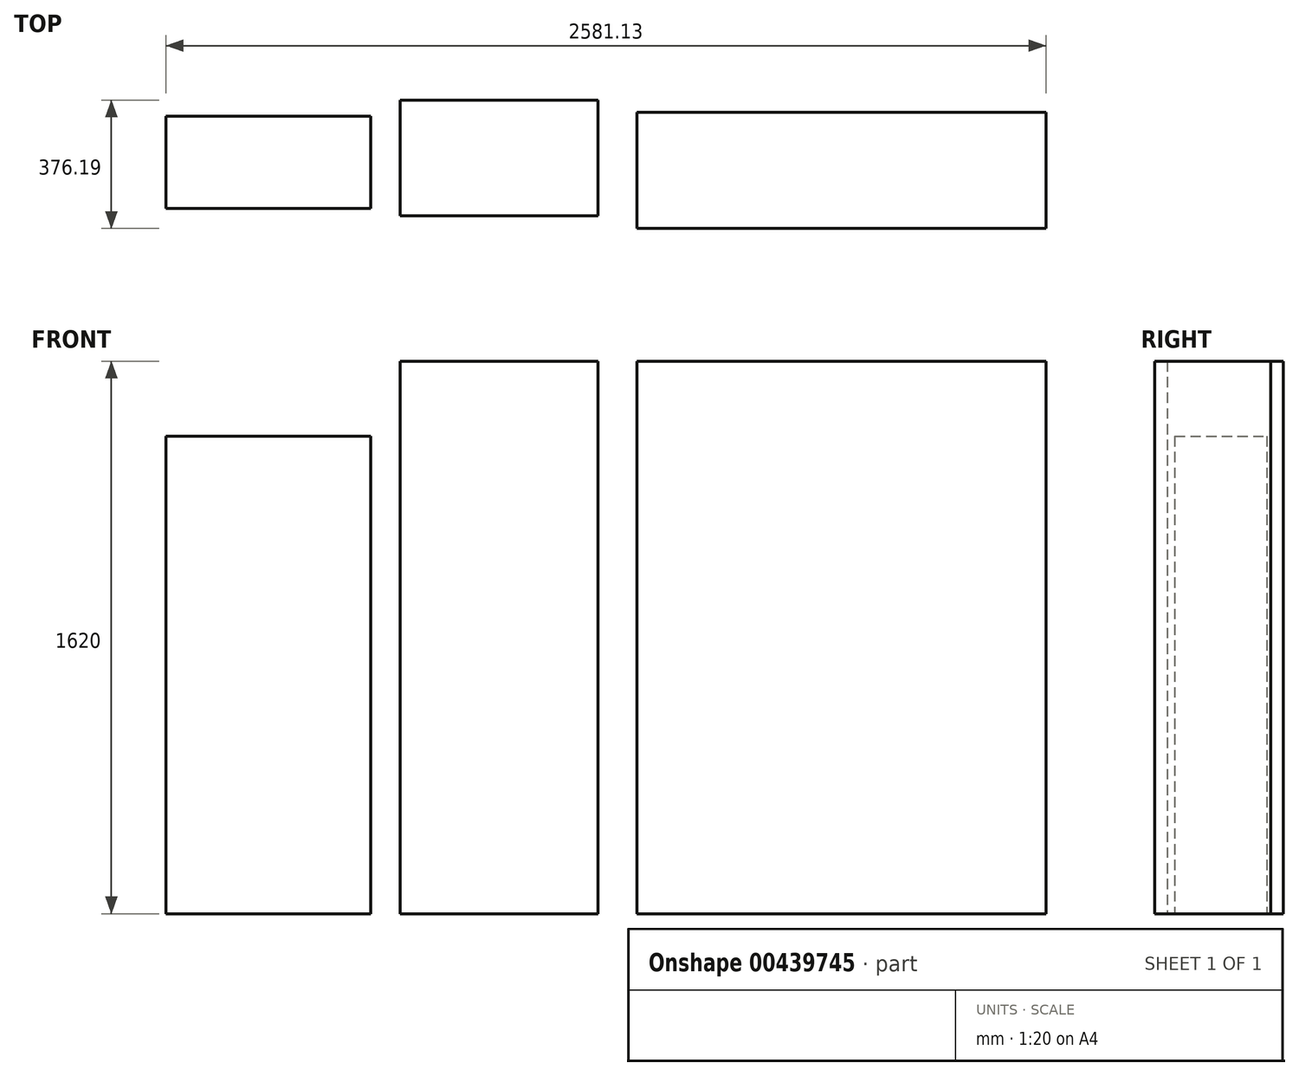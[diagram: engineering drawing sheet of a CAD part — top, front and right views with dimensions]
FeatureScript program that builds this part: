
annotation { "Feature Type Name" : "Feature", "Feature Type Description" : "" }
export const myFeature = defineFeature(function(context is Context, id is Id, definition is map)
    precondition{}
    {
        {
            var Q0;
            Q0=qCreatedBy(makeId("Top.planeOp"),FACE);
            var sketch = newSketch(context, id + "F0", { "sketchPlane" : qUnion([Q0])});
            skLineSegment(sketch, "E0.bottom", {"start": v(300, -135) * mm, "end": v(-300, -135) * mm});
            skLineSegment(sketch, "E0.top", {"start": v(300, 135) * mm, "end": v(-300, 135) * mm});
            skLineSegment(sketch, "E0.left", {"start": v(300, -135) * mm, "end": v(300, 135) * mm});
            skLineSegment(sketch, "E0.right", {"start": v(-300, -135) * mm, "end": v(-300, 135) * mm});
            skPoint(sketch, "E0.middle", {"position": v(0, 0) * mm});
            skSolve(sketch);
        }
        {
            var Q0;
            Q0 = qSketchRegion(id + "F0", true);
            extrude(context, id + "F1", {"entities" : qUnion([Q0]), "depth" : 1400 * mm});
        }
        {
            var Q0;
            Q0=makeQuery(id+"F1.opExtrude","CAP_FACE",FACE,{"disambiguationData":[OSD([sQuery(id+"F0.wireOp",EDGE,"E0.bottom"),sQuery(id+"F0.wireOp",EDGE,"E0.top"),sQuery(id+"F0.wireOp",EDGE,"E0.left"),sQuery(id+"F0.wireOp",EDGE,"E0.right")])],"isStart":true});
            var sketch = newSketch(context, id + "F2", { "sketchPlane" : qUnion([Q0])});
            skLineSegment(sketch, "E1.bottom", {"start": v(387.35, -182.9) * mm, "end": v(967.35, -182.9) * mm});
            skLineSegment(sketch, "E1.top", {"start": v(387.35, 157.1) * mm, "end": v(967.35, 157.1) * mm});
            skLineSegment(sketch, "E1.left", {"start": v(387.35, -182.9) * mm, "end": v(387.35, 157.1) * mm});
            skLineSegment(sketch, "E1.right", {"start": v(967.35, -182.9) * mm, "end": v(967.35, 157.1) * mm});
            skSolve(sketch);
        }
        {
            var Q0;
            Q0 = qSketchRegion(id + "F2", true);
            extrude(context, id + "F3", {"entities" : qUnion([Q0]), "oppositeDirection" : true, "depth" : 1620 * mm});
        }
        {
            var Q0;
            Q0=makeQuery(id+"F3.opExtrude","CAP_FACE",FACE,{"disambiguationData":[OSD([sQuery(id+"F2.wireOp",EDGE,"E1.bottom"),sQuery(id+"F2.wireOp",EDGE,"E1.top"),sQuery(id+"F2.wireOp",EDGE,"E1.left"),sQuery(id+"F2.wireOp",EDGE,"E1.right")])],"isStart":true});
            var sketch = newSketch(context, id + "F4", { "sketchPlane" : qUnion([Q0])});
            skLineSegment(sketch, "E2.bottom", {"start": v(1081.13, -146.71) * mm, "end": v(2281.13, -146.71) * mm});
            skLineSegment(sketch, "E2.top", {"start": v(1081.13, 193.29) * mm, "end": v(2281.13, 193.29) * mm});
            skLineSegment(sketch, "E2.left", {"start": v(1081.13, -146.71) * mm, "end": v(1081.13, 193.29) * mm});
            skLineSegment(sketch, "E2.right", {"start": v(2281.13, -146.71) * mm, "end": v(2281.13, 193.29) * mm});
            skSolve(sketch);
        }
        {
            var Q0;
            Q0=makeQuery(id+"F4.imprint","IMPRINT",FACE,{"disambiguationData":[TD([[makeQuery(id+"F4.imprint","IMPRINT",EDGE,{"derivedFrom":sQuery(id+"F4.wireOp",EDGE,"E2.bottom")}),1.0]])]});
            extrude(context, id + "F5", {"entities" : qUnion([Q0]), "oppositeDirection" : true, "depth" : 1620 * mm});
        }
    });
